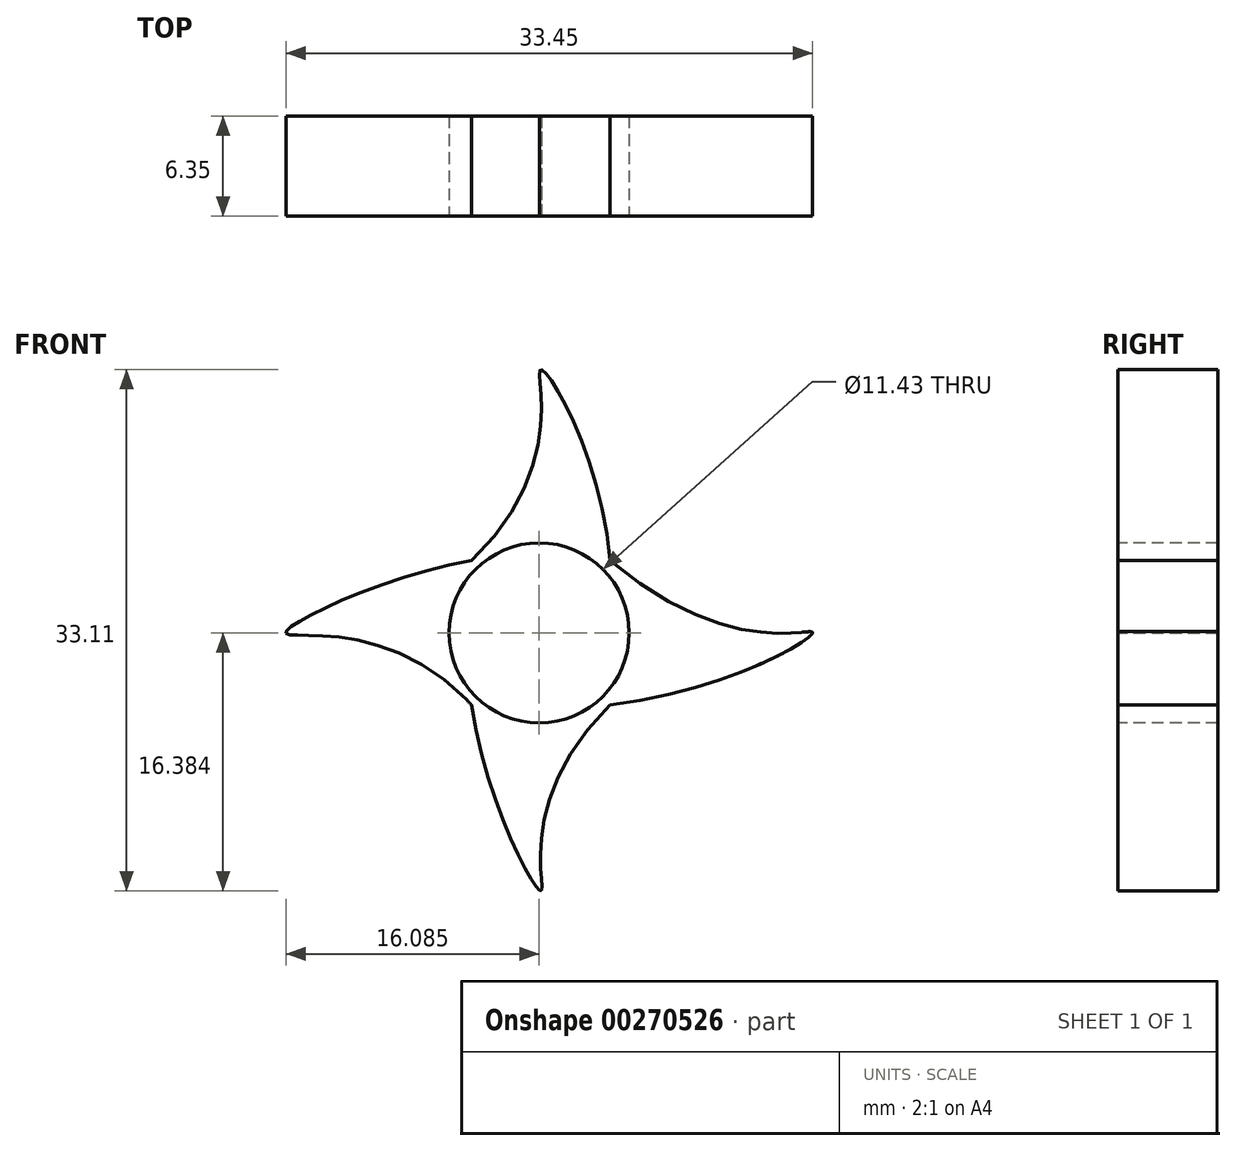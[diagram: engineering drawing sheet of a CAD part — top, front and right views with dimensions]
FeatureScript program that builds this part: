
annotation { "Feature Type Name" : "Feature", "Feature Type Description" : "" }
export const myFeature = defineFeature(function(context is Context, id is Id, definition is map)
    precondition{}
    {
        {
            var Q0;
            Q0=qCreatedBy(makeId("Front.planeOp"),FACE);
            var sketch = newSketch(context, id + "F0", { "sketchPlane" : qUnion([Q0])});
            skCircle(sketch, "E0", {"center": v(-40.2, 20.28) * mm, "radius": 6.35 * mm});
            skPoint(sketch, "E1", {"position": v(-46.55, 20.28) * mm});
            skPoint(sketch, "E2", {"position": v(-40.2, 26.63) * mm});
            skPoint(sketch, "E3", {"position": v(-33.85, 20.28) * mm});
            skPoint(sketch, "E4", {"position": v(-40.2, 13.93) * mm});
            skPoint(sketch, "E5", {"position": v(-44.59, 24.88) * mm});
            skPoint(sketch, "E6", {"position": v(-35.82, 24.88) * mm});
            skPoint(sketch, "E7", {"position": v(-35.82, 15.7) * mm});
            skPoint(sketch, "E8", {"position": v(-44.59, 15.7) * mm});
            skFitSpline(sketch, "E9", {"points": [v(-44.59, 24.88) * mm, v(-40.2, 37) * mm, v(-35.82, 24.88) * mm], "startDerivative": vector(37.44, 35.8) * mm, "endDerivative": vector(2.88, -38.87) * mm});
            skFitSpline(sketch, "E10", {"points": [v(-44.59, 15.7) * mm, v(-40.2, 3.9) * mm, v(-35.82, 15.7) * mm], "startDerivative": vector(5.12, -36.5) * mm, "endDerivative": vector(36.67, 36.5) * mm});
            skFitSpline(sketch, "E11", {"points": [v(-35.82, 24.88) * mm, v(-22.94, 20.28) * mm, v(-35.82, 15.7) * mm], "startDerivative": vector(45.64, -38.4) * mm, "endDerivative": vector(-45.64, -5.83) * mm});
            skFitSpline(sketch, "E12", {"points": [v(-44.59, 24.88) * mm, v(-56.4, 20.28) * mm, v(-44.59, 15.7) * mm], "startDerivative": vector(-33.5, -5.8) * mm, "endDerivative": vector(32.77, -34.81) * mm});
            skSolve(sketch);
        }
        {
            var Q0;
            {var subQ2=sQuery(id+"F0.wireOp",EDGE,"E0");var subQ6=sQuery(id+"F0.wireOp",EDGE,"E12");var subQ9=makeQuery(id+"F0.imprint","INTERSECT",VERTEX,{"derivedFrom":[subQ2,subQ6]});Q0=makeQuery(id+"F0.imprint","IMPRINT",FACE,{"disambiguationData":[TD([[makeQuery(id+"F0.imprint","IMPRINT",EDGE,{"disambiguationData":[TD([[subQ9,1.0]])],"derivedFrom":subQ2}),1.0]])]});}
            var Q1;
            {var subQ0=sQuery(id+"F0.wireOp",EDGE,"E9");Q1=makeQuery(id+"F0.imprint","IMPRINT",FACE,{"disambiguationData":[TD([[makeQuery(id+"F0.imprint","IMPRINT",EDGE,{"derivedFrom":subQ0}),-1.0]])]});}
            var Q2;
            {var subQ0=sQuery(id+"F0.wireOp",EDGE,"E12");var subQ1=sQuery(id+"F0.wireOp",EDGE,"E0");var subQ3=makeQuery(id+"F0.imprint","INTERSECT",VERTEX,{"derivedFrom":[subQ1,subQ0]});Q2=makeQuery(id+"F0.imprint","IMPRINT",FACE,{"disambiguationData":[TD([[makeQuery(id+"F0.imprint","IMPRINT",EDGE,{"disambiguationData":[TD([[subQ3,1.0]])],"derivedFrom":subQ1}),-1.0]])]});}
            var Q3;
            {var subQ0=sQuery(id+"F0.wireOp",EDGE,"E10");Q3=makeQuery(id+"F0.imprint","IMPRINT",FACE,{"disambiguationData":[TD([[makeQuery(id+"F0.imprint","IMPRINT",EDGE,{"derivedFrom":subQ0}),1.0]])]});}
            var Q4;
            {var subQ0=sQuery(id+"F0.wireOp",EDGE,"E11");Q4=makeQuery(id+"F0.imprint","IMPRINT",FACE,{"disambiguationData":[TD([[makeQuery(id+"F0.imprint","IMPRINT",EDGE,{"derivedFrom":subQ0}),-1.0]])]});}
            extrude(context, id + "F1", {"entities" : qUnion([Q0, Q1, Q2, Q3, Q4]), "depth" : 6.35 * mm});
        }
        {
            var Q0;
            Q0=makeQuery(id+"F1.opExtrude","CAP_FACE",FACE,{"disambiguationData":[OSD([sQuery(id+"F0.wireOp",EDGE,"E9"),sQuery(id+"F0.wireOp",EDGE,"E10"),sQuery(id+"F0.wireOp",EDGE,"E11"),sQuery(id+"F0.wireOp",EDGE,"E12")])],"isStart":false});
            var sketch = newSketch(context, id + "F2", { "sketchPlane" : qUnion([Q0])});
            skPoint(sketch, "E13", {"position": v(-40.3, 20.27) * mm});
            skSolve(sketch);
        }
        {
            var Q0;
            Q0=sQuery(id+"F2.wireOp",VERTEX,"E13");
            var Q1;
            Q1=makeQuery(id+"F1.opExtrude","SWEPT_BODY",BODY,{"disambiguationData":[OSD([sQuery(id+"F0.wireOp",EDGE,"E9"),sQuery(id+"F0.wireOp",EDGE,"E10"),sQuery(id+"F0.wireOp",EDGE,"E11"),sQuery(id+"F0.wireOp",EDGE,"E12")])]});
            hole(context, id + "F3", {"style" : HoleStyle.SIMPLE, "endStyle" : HoleEndStyle.BLIND, "holeDiameter" : 11.43 * mm, "holeDepth" : 25.4 * mm, "tappedDepth" : 12.7 * mm, "tapClearance" : 3, "locations" : qUnion([Q0]), "scope" : qUnion([Q1])});
        }
    });
